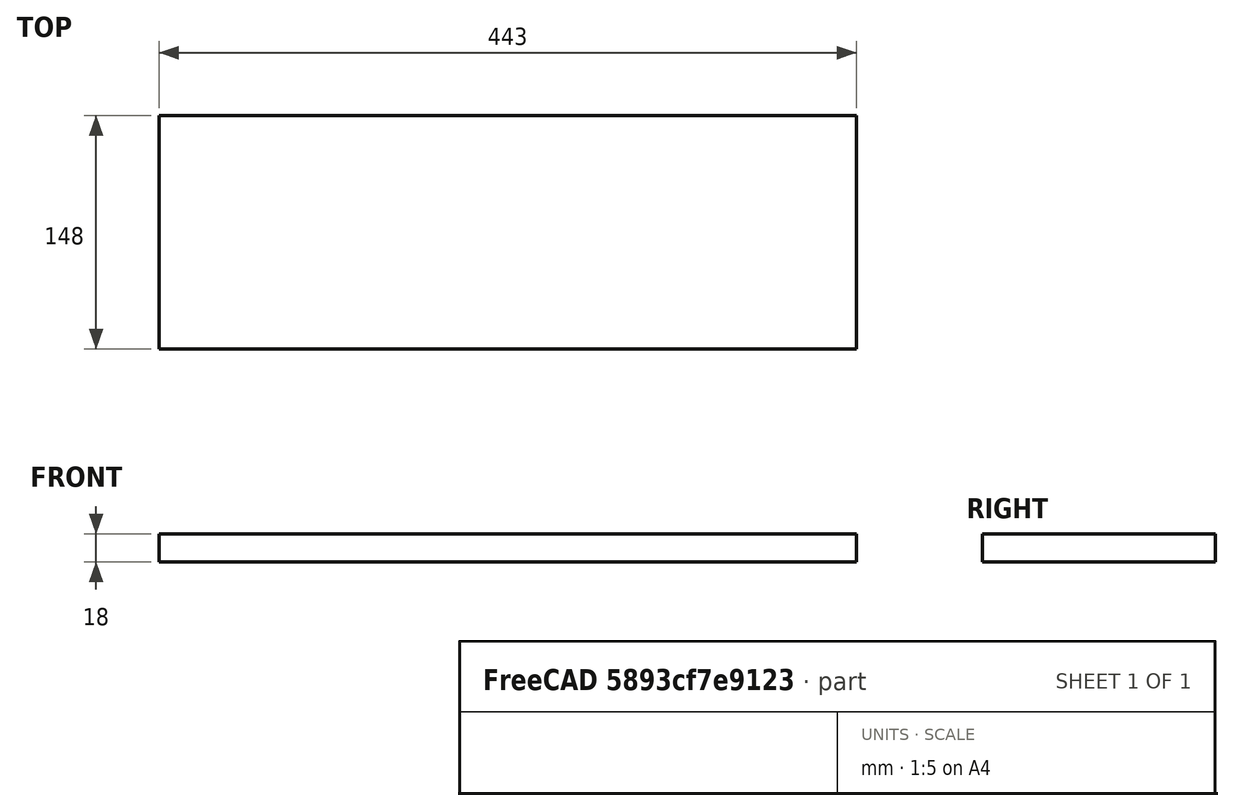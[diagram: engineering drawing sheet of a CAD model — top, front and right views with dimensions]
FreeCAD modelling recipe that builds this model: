
FCSTD DOCUMENT  (FreeCAD 0.17R13541 (Git))
Label: FaceInferieure
License: All rights reserved
LicenseURL: http://en.wikipedia.org/wiki/All_rights_reserved
objects: Sketcher::SketchObject×1, PartDesign::Pad×1, PartDesign::Body×1
note: 4 computed .brp shape members not serialized (recipe doc carries the construction recipe); baked Part::Feature solids carry a one-line shape summary decoded from their .brp

FEATURE [Sketcher::SketchObject] Sketch
  MapMode = 5
  Support = -> [XY_Plane]
  sketch-geometry (6):
    g0: LineSegment StartX=-221.5 StartY=74 StartZ=0 EndX=221.5 EndY=74 EndZ=0
    g1: LineSegment StartX=221.5 StartY=74 StartZ=0 EndX=221.5 EndY=-74 EndZ=0
    g2: LineSegment StartX=221.5 StartY=-74 StartZ=0 EndX=-221.5 EndY=-74 EndZ=0
    g3: LineSegment StartX=-221.5 StartY=-74 StartZ=0 EndX=-221.5 EndY=74 EndZ=0
    g4: LineSegment [constr] StartX=-221.5 StartY=74 StartZ=0 EndX=221.5 EndY=-74 EndZ=0
    g5: LineSegment [constr] StartX=-221.5 StartY=-74 StartZ=0 EndX=221.5 EndY=74 EndZ=0
  constraints (16):
    c: Coincident(g0,g1)
    c: Coincident(g1,g2)
    c: Coincident(g2,g3)
    c: Coincident(g3,g0)
    c: Horizontal(g0)
    c: Horizontal(g2)
    c: Vertical(g1)
    c: Vertical(g3)
    c: Coincident(g4,g0)
    c: Coincident(g4,g1)
    c: Coincident(g5,g2)
    c: Coincident(g5,g0)
    c: PointOnObject(g-1,g4)
    c: PointOnObject(g-1,g5)
    c: DistanceX(g0,g0) = 443  'Largeur a'
    c: DistanceY(g3,g3) = 148  'Profondeur b'
FEATURE [PartDesign::Pad] Pad
  Length = 18
  Length2 = 100
  Profile = -> Sketch
  Type = 0
FEATURE [PartDesign::Body] Body  label="Face superieure"
  Group = -> [Sketch,Pad]
  Origin = -> Origin
  Tip = -> Pad
